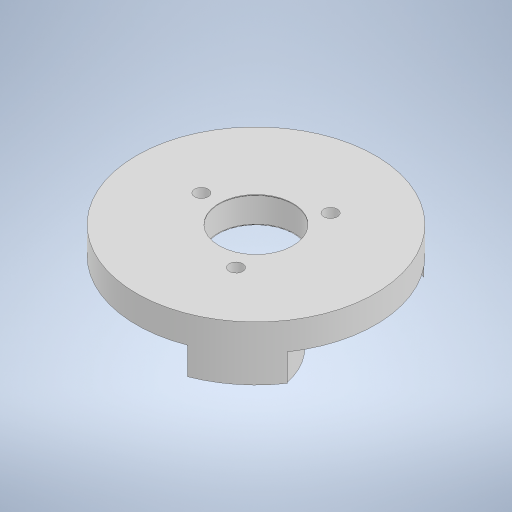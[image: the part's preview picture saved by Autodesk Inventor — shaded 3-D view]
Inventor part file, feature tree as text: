
AUTODESK INVENTOR PART (.ipt)
format: ipt  version: 2023.2 (Build 272271000, 271)  size: 512,000 bytes
history: native  units: in
note: dims shown in document units (in); Inventor stores cm internally (conversion verified against a paired STEP export)
features: thicken_offset x5, other x4, extrude x2, sketch x2, surface_op x1, plane x1
ambient origin geometry x8: Origin, YZ Plane, XZ Plane, XY Plane, X Axis, Y Axis, Z Axis, Center Point
bodies: Solid1 (feature_tree)
feature tree (15):
  extrude  "Extrusion1"  Depth=1.378in
  surface_op  "Sculpt1"
  plane  "Work Plane1"
  extrude  "Extrusion2"  Depth=0.0787in
  thicken_offset  "Thicken1"
  thicken_offset  "Thicken2"
  thicken_offset  "Thicken3"
  thicken_offset  "Thicken4"
  thicken_offset  "Thicken5"
  sketch  "Sketch1"  dims[d0=0.1969in d1=1.378in]
  sketch  "Sketch2"  dims[d2=0.6299in d3=0.0787in d4=1.1811in d6=360.0deg d8=0.315in d9=0.0in d10=0.0625in d11=0.6299in d12=1.378in d13=1.1811in d15=360.0deg d17=1.1811in d19=360.0deg d21=0.1575in d22=0.0in d23=2.3622in d25=360.0deg d27=0.0039in d28=0.0039in d29=0.0039in d30=0.0039in d31=0.0039in d32=0.0039in d33=0.0039in d34=0.0039in d35=0.0039in d36=0.0039in]
  other  "Composite1"
  other  "Srf1"
  other  "Flash Hobby D3530 1100KV.iam"
  other  "Body - Basic:1"
